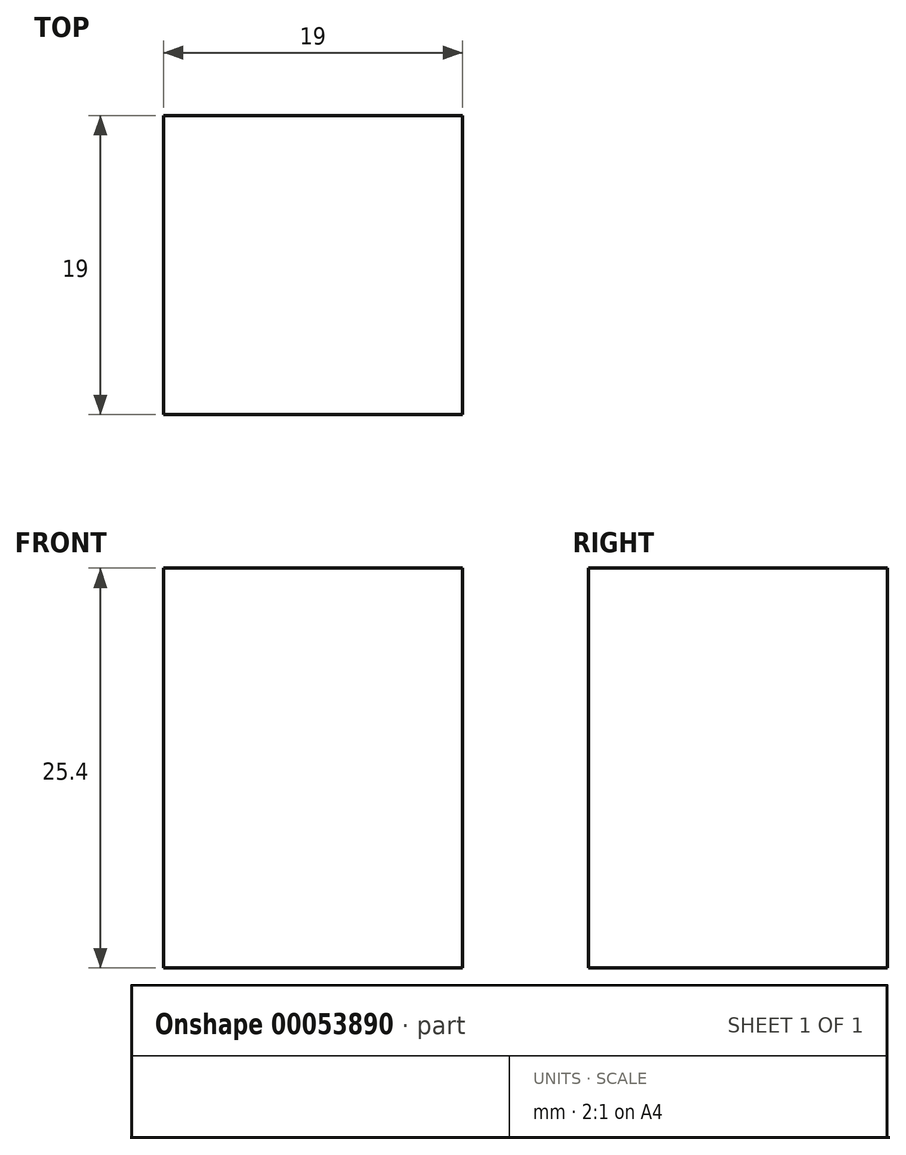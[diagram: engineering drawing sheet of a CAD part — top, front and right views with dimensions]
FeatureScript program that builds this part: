
annotation { "Feature Type Name" : "Feature", "Feature Type Description" : "" }
export const myFeature = defineFeature(function(context is Context, id is Id, definition is map)
    precondition{}
    {
        {
            var Q0;
            Q0=qCreatedBy(makeId("Top.planeOp"),FACE);
            var sketch = newSketch(context, id + "F0", { "sketchPlane" : qUnion([Q0])});
            skLineSegment(sketch, "E0.bottom", {"start": v(-55.78, 0) * mm, "end": v(-36.78, 0) * mm});
            skLineSegment(sketch, "E0.top", {"start": v(-55.78, 184) * mm, "end": v(-36.78, 184) * mm});
            skLineSegment(sketch, "E0.left", {"start": v(-55.78, 0) * mm, "end": v(-55.78, 184) * mm});
            skLineSegment(sketch, "E0.right", {"start": v(-36.78, 0) * mm, "end": v(-36.78, 184) * mm});
            skLineSegment(sketch, "E1.left", {"start": v(-36.78, 0) * mm, "end": v(-36.78, 19) * mm});
            skSolve(sketch);
        }
        {
            var Q0;
            Q0=makeQuery(id+"F0.imprint","IMPRINT",FACE,{"disambiguationData":[TD([[makeQuery(id+"F0.imprint","IMPRINT",EDGE,{"derivedFrom":sQuery(id+"F0.wireOp",EDGE,"E0.bottom")}),1.0]])]});
            var sketch = newSketch(context, id + "F1", { "sketchPlane" : qUnion([Q0])});
            skLineSegment(sketch, "E2.bottom", {"start": v(-32.43, 0) * mm, "end": v(-13.43, 0) * mm});
            skLineSegment(sketch, "E2.top", {"start": v(-32.43, 19) * mm, "end": v(-13.43, 19) * mm});
            skLineSegment(sketch, "E2.left", {"start": v(-32.43, 0) * mm, "end": v(-32.43, 19) * mm});
            skLineSegment(sketch, "E2.right", {"start": v(-13.43, 0) * mm, "end": v(-13.43, 19) * mm});
            skSolve(sketch);
        }
        {
            var Q0;
            Q0 = qConstructionFilter(qBodyType(qCreatedBy(id + "F1" ,EDGE), BodyType.WIRE), ConstructionObject.NO);
            extrude(context, id + "F2", {"bodyType" : ToolBodyType.SURFACE, "surfaceEntities" : qUnion([Q0]), "depth" : 25.4 * mm});
        }
    });
